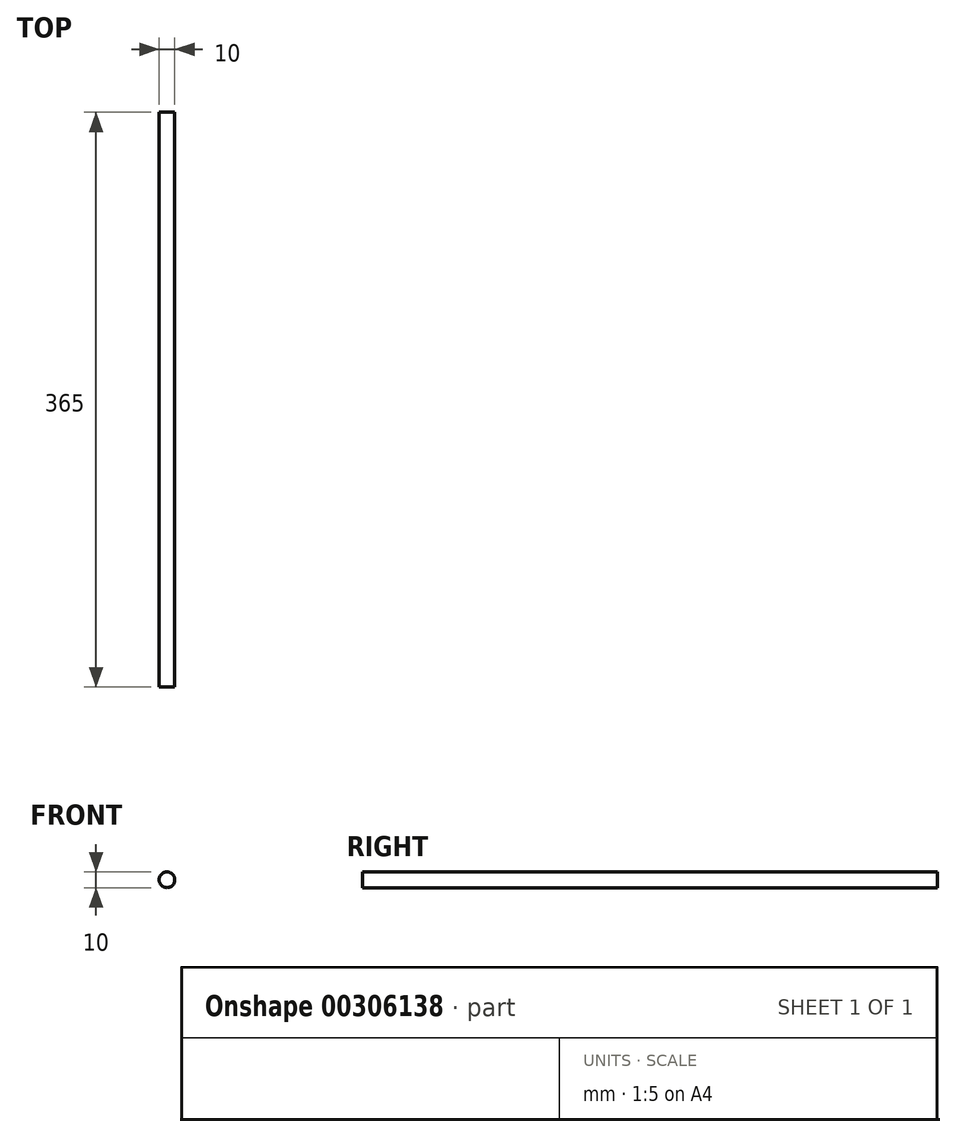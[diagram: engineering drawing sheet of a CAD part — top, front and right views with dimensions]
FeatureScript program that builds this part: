
annotation { "Feature Type Name" : "Feature", "Feature Type Description" : "" }
export const myFeature = defineFeature(function(context is Context, id is Id, definition is map)
    precondition{}
    {
        {
            var Q0;
            Q0=qCreatedBy(makeId("Front.planeOp"),FACE);
            var sketch = newSketch(context, id + "F0", { "sketchPlane" : qUnion([Q0])});
            skCircle(sketch, "E0", {"center": v(0, 0) * mm, "radius": 5 * mm});
            skSolve(sketch);
        }
        {
            var Q0;
            Q0=makeQuery(id+"F0.imprint","IMPRINT",FACE,{"disambiguationData":[TD([[makeQuery(id+"F0.imprint","IMPRINT",EDGE,{"derivedFrom":sQuery(id+"F0.wireOp",EDGE,"E0")}),1.0]])]});
            extrude(context, id + "F1", {"entities" : qUnion([Q0]), "oppositeDirection" : true, "depth" : 365 * mm});
        }
    });
